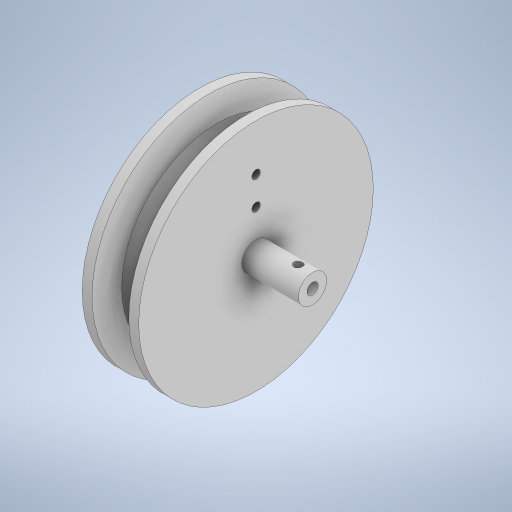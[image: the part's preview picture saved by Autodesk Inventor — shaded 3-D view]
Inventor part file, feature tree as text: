
AUTODESK INVENTOR PART (.ipt)
format: ipt  version: 2023 (Build 270158000, 158)  size: 316,928 bytes
history: native  units: mm
features: sketch x6, extrude x4, other x3, thread x3, revolve x1
ambient origin geometry x8: Origin, YZ Plane, XZ Plane, XY Plane, X Axis, Y Axis, Z Axis, Center Point
bodies: Body1 (feature_tree)
feature tree (17):
  other  "Твердое тело1"
  revolve  "Вращение1"
  extrude  "Выдавливание1"  Depth=20.0mm
  extrude  "Выдавливание2"  Depth=41.5mm
  sketch  "Эскиз4"
  other  "РабПлоскость1"
  extrude  "Выдавливание3"  Depth=6.0mm
  thread  "Резьба1"
  other  "РабПлоскость2"
  extrude  "Выдавливание4"  Depth=8.0mm
  thread  "Резьба2"
  thread  "Резьба3"
  sketch  "Эскиз1"
  sketch  "Эскиз2"
  sketch  "Эскиз3"
  sketch  "Эскиз5"
  sketch  "Эскиз6"
